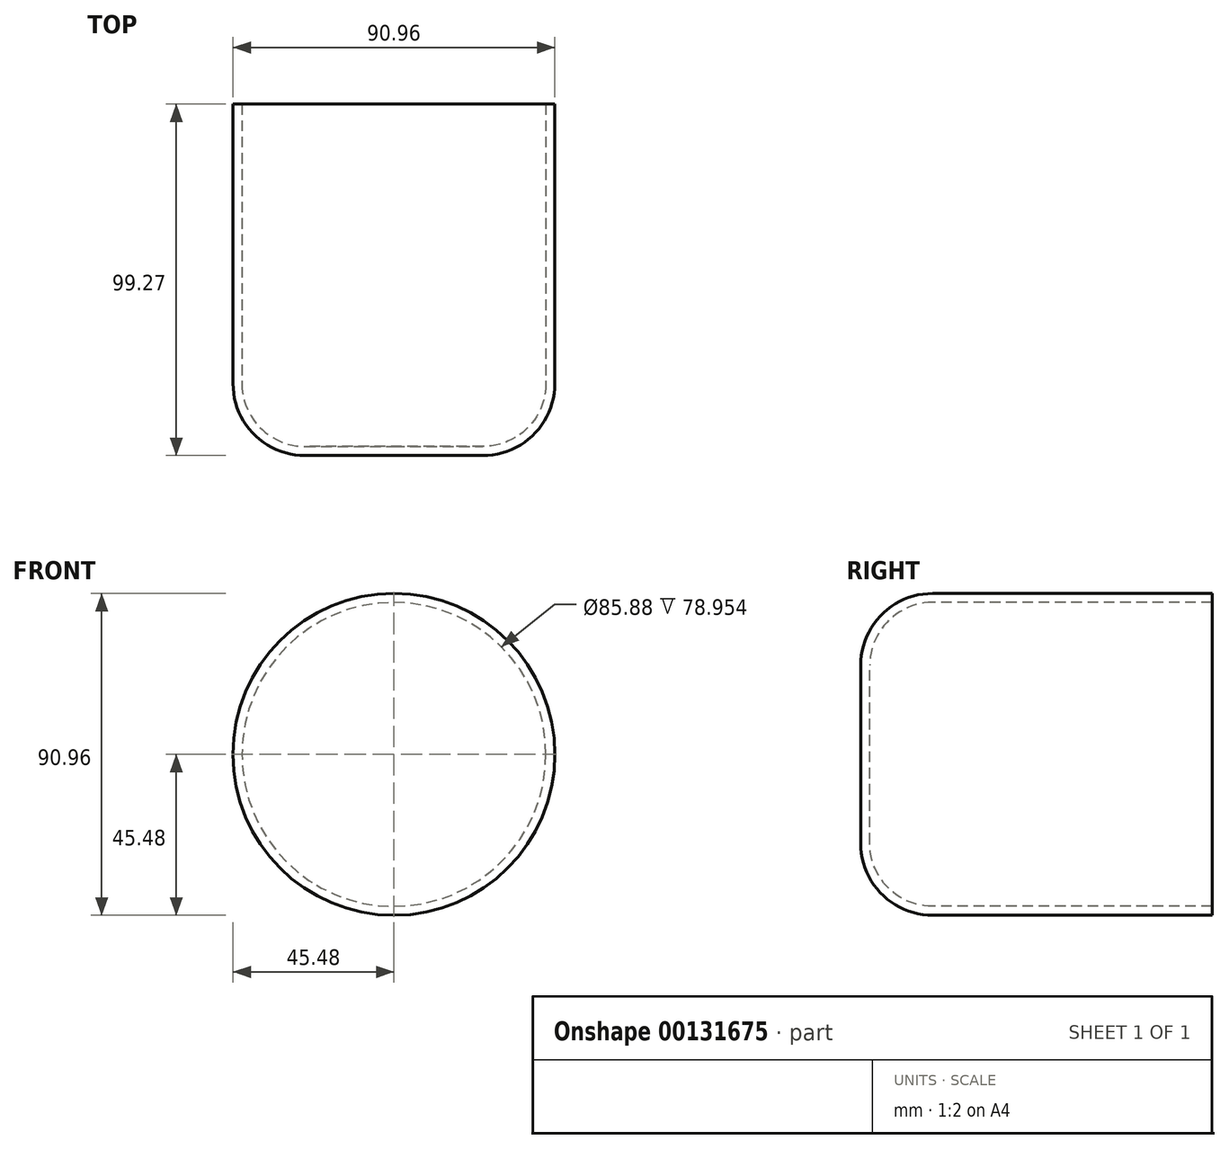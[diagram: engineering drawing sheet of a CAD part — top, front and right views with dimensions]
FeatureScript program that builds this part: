
annotation { "Feature Type Name" : "Feature", "Feature Type Description" : "" }
export const myFeature = defineFeature(function(context is Context, id is Id, definition is map)
    precondition{}
    {
        {
            var Q0;
            Q0=qCreatedBy(makeId("Right.planeOp"),FACE);
            var sketch = newSketch(context, id + "F0", { "sketchPlane" : qUnion([Q0])});
            skLineSegment(sketch, "E0.bottom", {"start": v(0, 0) * mm, "end": v(99.27, 0) * mm});
            skLineSegment(sketch, "E0.top", {"start": v(0, 45.48) * mm, "end": v(99.27, 45.48) * mm});
            skLineSegment(sketch, "E0.left", {"start": v(0, 0) * mm, "end": v(0, 45.48) * mm});
            skLineSegment(sketch, "E0.right", {"start": v(99.27, 0) * mm, "end": v(99.27, 45.48) * mm});
            skSolve(sketch);
        }
        {
            var Q0;
            Q0 = qSketchRegion(id + "F0", true);
            var Q1;
            Q1=sQuery(id+"F0.wireOp",EDGE,"E0.bottom");
            revolve(context, id + "F1", {"entities" : qUnion([Q0]), "axis" : qUnion([Q1]), "revolveType" : RevolveType.FULL});
        }
        {
            var Q0;
            Q0=makeQuery(id+"F1.opRevolve","SWEPT_FACE",FACE,{"disambiguationData":[OSD([sQuery(id+"F0.wireOp",EDGE,"E0.left")])]});
            fillet(context, id + "F2", {"entities" : qUnion([Q0]), "radius" : 20.32 * mm, "tangentPropagation" : true, "allowEdgeOverflow" : false});
        }
        {
            var Q0;
            Q0=makeQuery(id+"F1.opRevolve","SWEPT_FACE",FACE,{"disambiguationData":[OSD([sQuery(id+"F0.wireOp",EDGE,"E0.right")])]});
            shell(context, id + "F3", {"entities" : qUnion([Q0]), "thickness" : 2.54 * mm});
        }
    });
